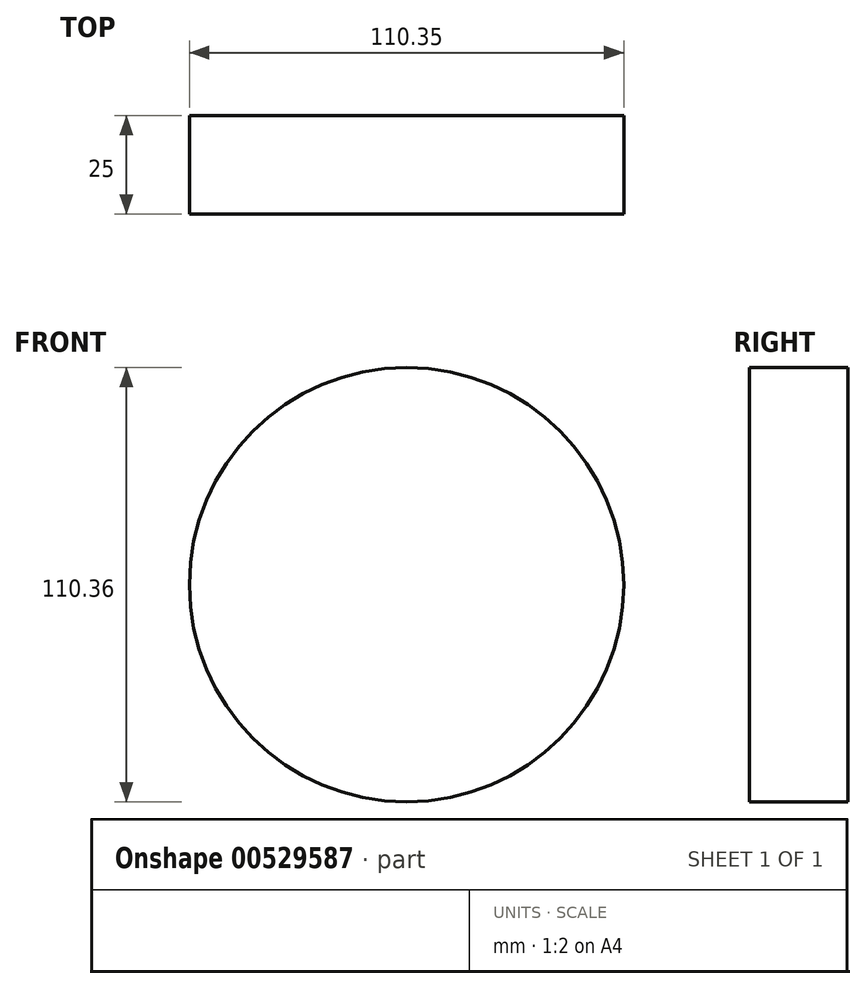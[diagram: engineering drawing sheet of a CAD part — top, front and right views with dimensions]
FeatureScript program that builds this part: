
annotation { "Feature Type Name" : "Feature", "Feature Type Description" : "" }
export const myFeature = defineFeature(function(context is Context, id is Id, definition is map)
    precondition{}
    {
        {
            var Q0;
            Q0=qCreatedBy(makeId("Front.planeOp"),FACE);
            var sketch = newSketch(context, id + "F0", { "sketchPlane" : qUnion([Q0])});
            skCircle(sketch, "E0", {"center": v(-10.8, 14.14) * mm, "radius": 55.18 * mm});
            skSolve(sketch);
        }
        {
            var Q0;
            Q0=makeQuery(id+"F0.imprint","IMPRINT",FACE,{"disambiguationData":[TD([[makeQuery(id+"F0.imprint","IMPRINT",EDGE,{"derivedFrom":sQuery(id+"F0.wireOp",EDGE,"E0")}),1.0]])]});
            extrude(context, id + "F1", {"entities" : qUnion([Q0]), "depth" : 25 * mm, "offsetDistance" : 25 * mm});
        }
    });
